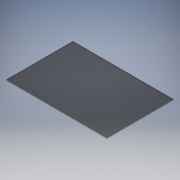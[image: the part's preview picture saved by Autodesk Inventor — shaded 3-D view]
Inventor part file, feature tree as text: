
AUTODESK INVENTOR PART (.ipt)
format: ipt  version: 2016 (Build 200138000, 138)  size: 102,400 bytes
history: native  units: mm
features: extrude x1, sketch x1
ambient origin geometry x8: Origin, YZ Plane, XZ Plane, XY Plane, X Axis, Y Axis, Z Axis, Center Point
bodies: 实体1 (feature_tree)
feature tree (2):
  extrude  "拉伸1"  Depth=500.0mm
  sketch  "草图1"  dims[d0=755.0mm d1=500.0mm d2=5.0mm d3=0.0mm]
